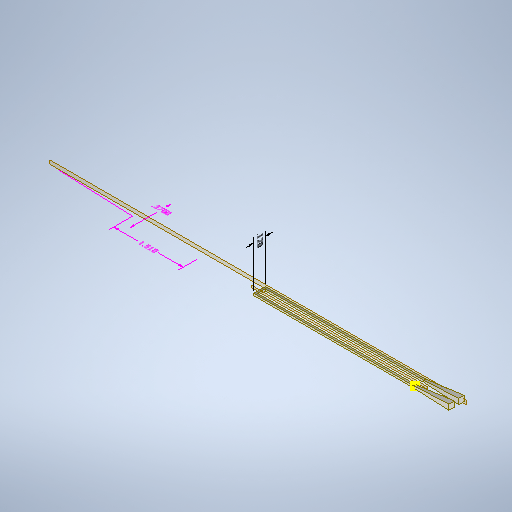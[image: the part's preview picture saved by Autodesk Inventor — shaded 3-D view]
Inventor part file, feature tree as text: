
AUTODESK INVENTOR PART (.ipt)
format: ipt  version: 2025.2 (Build 292293000, 293)  size: 313,856 bytes
history: native  units: in
note: dims shown in document units (in); Inventor stores cm internally (conversion verified against a paired STEP export)
features: other x5, plane x4, sketch x4, sweep x1, loft x1, mirror x1, projected_geometry x1
ambient origin geometry x8: Origin, YZ Plane, XZ Plane, XY Plane, X Axis, Y Axis, Z Axis, Center Point
bodies: Solid1 (feature_tree)
feature tree (17):
  other  "Annotations"
  sweep  "Sweep1"
  plane  "Work Plane1"
  plane  "Work Plane2"
  plane  "Work Plane4"
  sketch  "Sketch15"  dims[d86=-0.1175in]
  sketch  "Sketch16"  dims[d89=0.1in d90=0.0in d91=0.0in d92=0.0in d98=0.02in d99=0.02in d100=0.055in d102=0.055in d104=0.0in d109=0.0in d110=90.0deg d111=0.0in d112=90.0deg d116=-0.06in d113=0.0in d114=0.3937in d115=0.12in d42=0.2341in d43=0.169in d44=0.37in d48=0.2141in d49=0.2512in d50=1.51in]
  loft  "Loft3"
  plane  "Work Plane5"
  mirror  "Mirror3"
  sketch  "Sketch1"  dims[d6=0.0in d7=0.0in d11=0.375in d19=-0.25in]
  sketch  "Sketch2"  dims[d69=1.625in d70=1.625in]
  projected_geometry  "Projected Loop1"
  other  "Edges4"
  other  "Linear Dimension 1"
  other  "Linear Dimension 3"
  other  "Linear Dimension 4"
